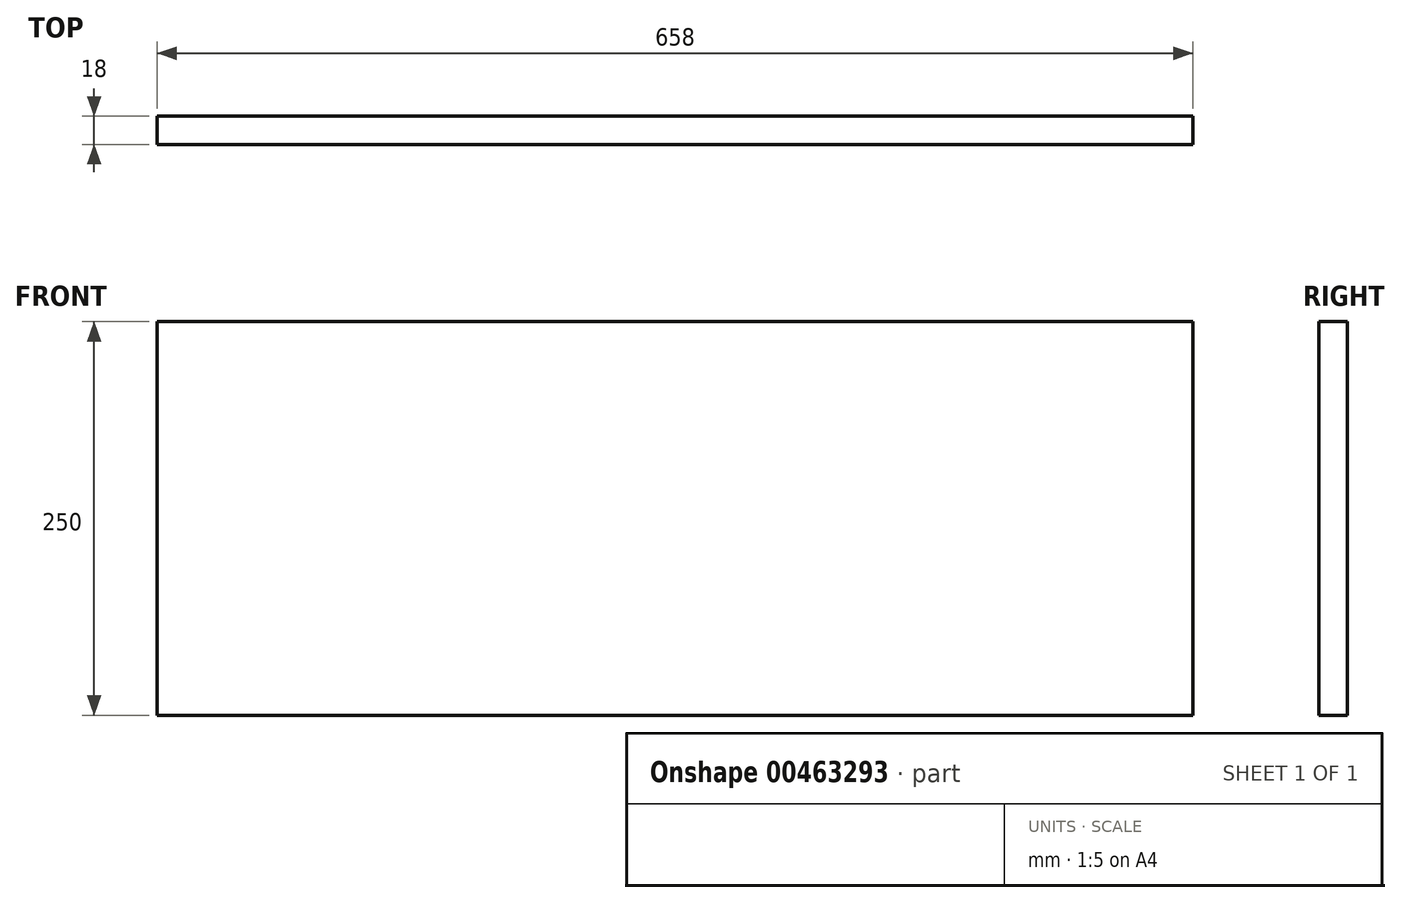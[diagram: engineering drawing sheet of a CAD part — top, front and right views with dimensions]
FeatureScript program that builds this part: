
annotation { "Feature Type Name" : "Feature", "Feature Type Description" : "" }
export const myFeature = defineFeature(function(context is Context, id is Id, definition is map)
    precondition{}
    {
        {
            var Q0;
            Q0=qCreatedBy(makeId("Front.planeOp"),FACE);
            var sketch = newSketch(context, id + "F0", { "sketchPlane" : qUnion([Q0])});
            skLineSegment(sketch, "E0.bottom", {"start": v(0, 0) * mm, "end": v(658, 0) * mm});
            skLineSegment(sketch, "E0.top", {"start": v(0, 250) * mm, "end": v(658, 250) * mm});
            skLineSegment(sketch, "E0.left", {"start": v(0, 0) * mm, "end": v(0, 250) * mm});
            skLineSegment(sketch, "E0.right", {"start": v(658, 0) * mm, "end": v(658, 250) * mm});
            skSolve(sketch);
        }
        {
            var Q0;
            Q0 = qSketchRegion(id + "F0", true);
            extrude(context, id + "F1", {"entities" : qUnion([Q0]), "depth" : 18 * mm});
        }
    });
